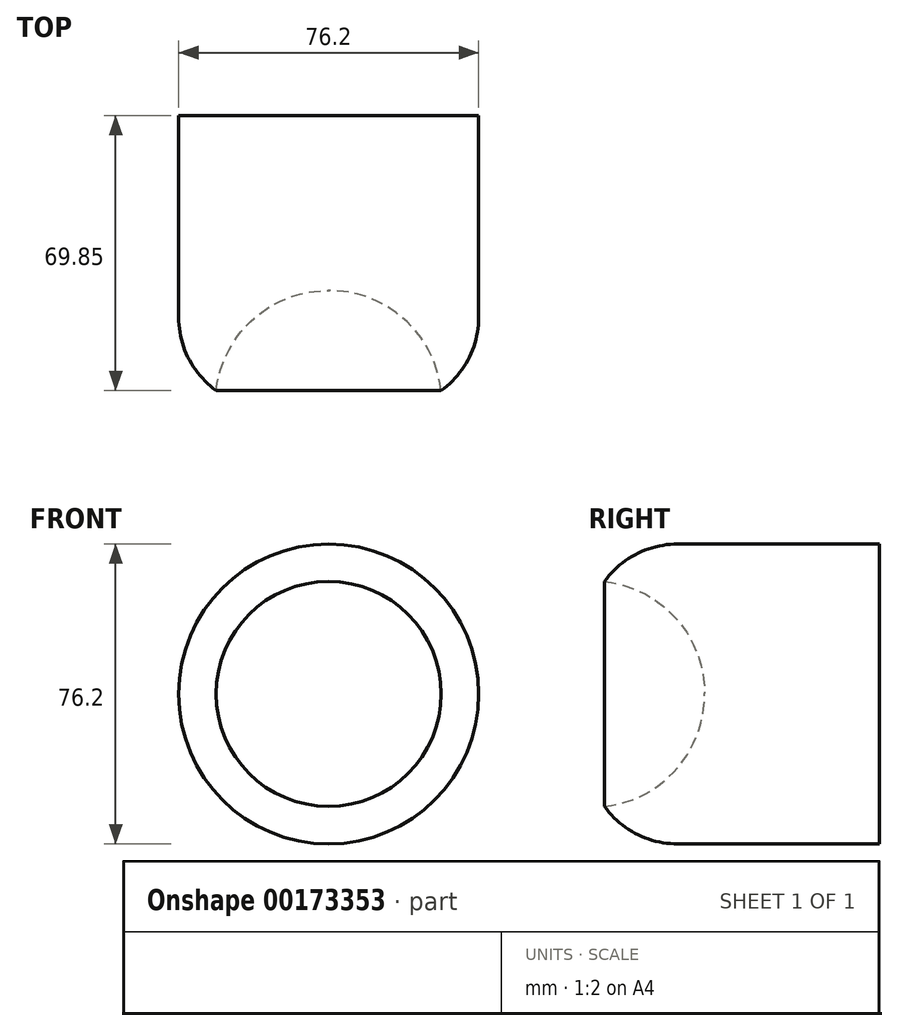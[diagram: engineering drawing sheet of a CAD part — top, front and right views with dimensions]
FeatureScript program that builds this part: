
annotation { "Feature Type Name" : "Feature", "Feature Type Description" : "" }
export const myFeature = defineFeature(function(context is Context, id is Id, definition is map)
    precondition{}
    {
        {
            var Q0;
            Q0=qCreatedBy(makeId("Front.planeOp"),FACE);
            var sketch = newSketch(context, id + "F0", { "sketchPlane" : qUnion([Q0])});
            skCircle(sketch, "E0", {"center": v(0, 0) * mm, "radius": 38.1 * mm});
            skSolve(sketch);
        }
        {
            var Q0;
            Q0=makeQuery(id+"F0.imprint","IMPRINT",FACE,{"disambiguationData":[TD([[makeQuery(id+"F0.imprint","IMPRINT",EDGE,{"derivedFrom":sQuery(id+"F0.wireOp",EDGE,"E0")}),1.0]])]});
            extrude(context, id + "F1", {"entities" : qUnion([Q0]), "depth" : 69.85 * mm});
        }
        {
            var Q0;
            Q0=makeQuery(id+"F1.opExtrude","CAP_FACE",FACE,{"disambiguationData":[OSD([sQuery(id+"F0.wireOp",EDGE,"E0")])],"isStart":false});
            var sketch = newSketch(context, id + "F2", { "sketchPlane" : qUnion([Q0])});
            skCircle(sketch, "E1", {"center": v(0, 0) * mm, "radius": 28.58 * mm});
            skSolve(sketch);
        }
        {
            var Q0;
            Q0=makeQuery(id+"F2.imprint","IMPRINT",FACE,{"disambiguationData":[TD([[makeQuery(id+"F2.imprint","IMPRINT",EDGE,{"derivedFrom":sQuery(id+"F2.wireOp",EDGE,"E1")}),1.0]])]});
            extrude(context, id + "F3", {"entities" : qUnion([Q0]), "operationType" : NewBodyOperationType.REMOVE, "oppositeDirection" : true, "depth" : 25.4 * mm});
        }
        {
            var Q0;
            Q0=makeQuery(id+"F3.boolean.opBoolean","COPY",EDGE,{"derivedFrom":makeQuery(id+"F3.opExtrude","CAP_EDGE",EDGE,{"disambiguationData":[OSD([sQuery(id+"F2.wireOp",EDGE,"E1")])],"isStart":false})});
            fillet(context, id + "F4", {"entities" : qUnion([Q0]), "radius" : 28.6 * mm, "tangentPropagation" : true, "allowEdgeOverflow" : false});
        }
        {
            var Q0;
            Q0=makeQuery(id+"F1.opExtrude","CAP_EDGE",EDGE,{"disambiguationData":[OSD([sQuery(id+"F0.wireOp",EDGE,"E0")])],"isStart":false});
            fillet(context, id + "F5", {"entities" : qUnion([Q0]), "radius" : 22.86 * mm, "tangentPropagation" : true, "allowEdgeOverflow" : false});
        }
    });
